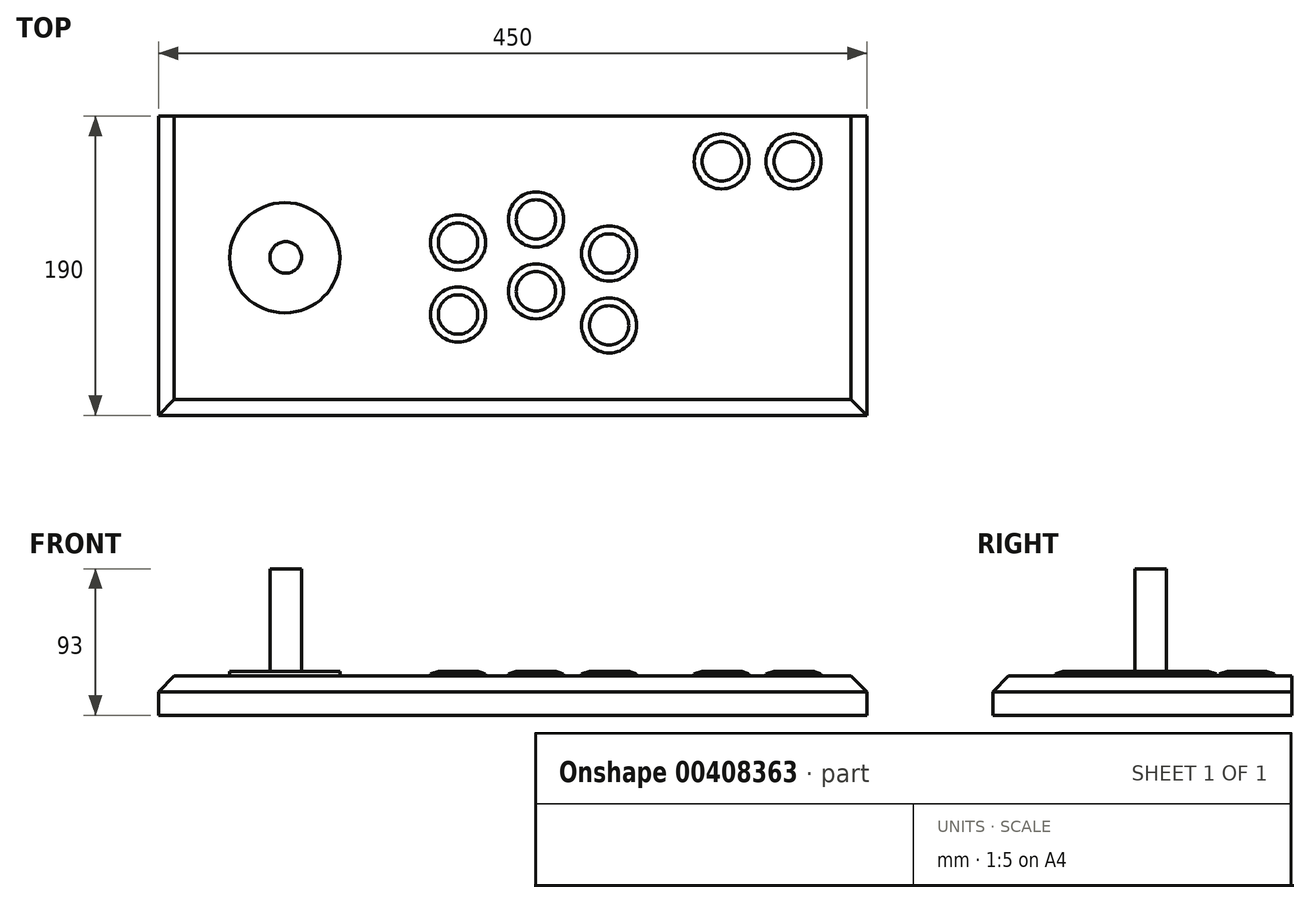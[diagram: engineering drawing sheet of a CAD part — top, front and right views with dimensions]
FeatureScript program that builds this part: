
annotation { "Feature Type Name" : "Feature", "Feature Type Description" : "" }
export const myFeature = defineFeature(function(context is Context, id is Id, definition is map)
    precondition{}
    {
        {
            var Q0;
            Q0=qCreatedBy(makeId("Top.planeOp"),FACE);
            var sketch = newSketch(context, id + "F0", { "sketchPlane" : qUnion([Q0])});
            skLineSegment(sketch, "E0", {"start": v(-232.6, -81.18) * mm, "end": v(217.4, -81.18) * mm});
            skLineSegment(sketch, "E1", {"start": v(-232.6, -81.18) * mm, "end": v(-232.6, 108.82) * mm});
            skLineSegment(sketch, "E2", {"start": v(-232.6, 108.82) * mm, "end": v(217.4, 108.82) * mm});
            skLineSegment(sketch, "E3", {"start": v(217.4, -81.18) * mm, "end": v(217.4, 108.82) * mm});
            skSolve(sketch);
        }
        {
            var Q0;
            Q0=makeQuery(id+"F0.imprint","IMPRINT",FACE,{"disambiguationData":[TD([[makeQuery(id+"F0.imprint","IMPRINT",EDGE,{"derivedFrom":sQuery(id+"F0.wireOp",EDGE,"E0")}),1.0]])]});
            extrude(context, id + "F1", {"entities" : qUnion([Q0]), "depth" : 25 * mm});
        }
        {
            var Q0;
            Q0=makeQuery(id+"F1.opExtrude","CAP_EDGE",EDGE,{"disambiguationData":[OSD([sQuery(id+"F0.wireOp",EDGE,"E1")])],"isStart":false});
            var Q1;
            Q1=makeQuery(id+"F1.opExtrude","CAP_EDGE",EDGE,{"disambiguationData":[OSD([sQuery(id+"F0.wireOp",EDGE,"E3")])],"isStart":false});
            var Q2;
            Q2=makeQuery(id+"F1.opExtrude","CAP_EDGE",EDGE,{"disambiguationData":[OSD([sQuery(id+"F0.wireOp",EDGE,"E0")])],"isStart":false});
            chamfer(context, id + "F2", {"entities" : qUnion([Q0, Q1, Q2]), "width" : 10 * mm, "tangentPropagation" : true});
        }
        {
            var Q0;
            Q0=makeQuery(id+"F1.opExtrude","CAP_FACE",FACE,{"disambiguationData":[OSD([sQuery(id+"F0.wireOp",EDGE,"E0"),sQuery(id+"F0.wireOp",EDGE,"E1"),sQuery(id+"F0.wireOp",EDGE,"E2"),sQuery(id+"F0.wireOp",EDGE,"E3")])],"isStart":false});
            var sketch = newSketch(context, id + "F3", { "sketchPlane" : qUnion([Q0])});
            skCircle(sketch, "E4", {"center": v(-152.3, 18.92) * mm, "radius": 35 * mm});
            skCircle(sketch, "E5", {"center": v(-42.27, 28.55) * mm, "radius": 17.5 * mm});
            skCircle(sketch, "E6", {"center": v(-42.27, -17.12) * mm, "radius": 17.5 * mm});
            skCircle(sketch, "E7", {"center": v(7.22, 43.26) * mm, "radius": 17.5 * mm});
            skCircle(sketch, "E8", {"center": v(7.22, -2.4) * mm, "radius": 17.5 * mm});
            skCircle(sketch, "E9", {"center": v(53.66, 21.62) * mm, "radius": 17.5 * mm});
            skCircle(sketch, "E10", {"center": v(53.66, -24.05) * mm, "radius": 17.5 * mm});
            skCircle(sketch, "E11", {"center": v(170.84, 80.17) * mm, "radius": 17.5 * mm});
            skCircle(sketch, "E12", {"center": v(125.17, 80.17) * mm, "radius": 17.5 * mm});
            skSolve(sketch);
        }
        {
            var Q0;
            Q0=makeQuery(id+"F3.imprint","IMPRINT",FACE,{"disambiguationData":[TD([[makeQuery(id+"F3.imprint","IMPRINT",EDGE,{"derivedFrom":sQuery(id+"F3.wireOp",EDGE,"E4")}),1.0]])]});
            var Q1;
            Q1=makeQuery(id+"F3.imprint","IMPRINT",FACE,{"disambiguationData":[TD([[makeQuery(id+"F3.imprint","IMPRINT",EDGE,{"derivedFrom":sQuery(id+"F3.wireOp",EDGE,"E5")}),1.0]])]});
            var Q2;
            Q2=makeQuery(id+"F3.imprint","IMPRINT",FACE,{"disambiguationData":[TD([[makeQuery(id+"F3.imprint","IMPRINT",EDGE,{"derivedFrom":sQuery(id+"F3.wireOp",EDGE,"E6")}),1.0]])]});
            var Q3;
            Q3=makeQuery(id+"F3.imprint","IMPRINT",FACE,{"disambiguationData":[TD([[makeQuery(id+"F3.imprint","IMPRINT",EDGE,{"derivedFrom":sQuery(id+"F3.wireOp",EDGE,"E7")}),1.0]])]});
            var Q4;
            Q4=makeQuery(id+"F3.imprint","IMPRINT",FACE,{"disambiguationData":[TD([[makeQuery(id+"F3.imprint","IMPRINT",EDGE,{"derivedFrom":sQuery(id+"F3.wireOp",EDGE,"E8")}),1.0]])]});
            var Q5;
            Q5=makeQuery(id+"F3.imprint","IMPRINT",FACE,{"disambiguationData":[TD([[makeQuery(id+"F3.imprint","IMPRINT",EDGE,{"derivedFrom":sQuery(id+"F3.wireOp",EDGE,"E9")}),1.0]])]});
            var Q6;
            Q6=makeQuery(id+"F3.imprint","IMPRINT",FACE,{"disambiguationData":[TD([[makeQuery(id+"F3.imprint","IMPRINT",EDGE,{"derivedFrom":sQuery(id+"F3.wireOp",EDGE,"E11")}),1.0]])]});
            var Q7;
            Q7=makeQuery(id+"F3.imprint","IMPRINT",FACE,{"disambiguationData":[TD([[makeQuery(id+"F3.imprint","IMPRINT",EDGE,{"derivedFrom":sQuery(id+"F3.wireOp",EDGE,"E12")}),1.0]])]});
            var Q8;
            Q8=makeQuery(id+"F3.imprint","IMPRINT",FACE,{"disambiguationData":[TD([[makeQuery(id+"F3.imprint","IMPRINT",EDGE,{"derivedFrom":sQuery(id+"F3.wireOp",EDGE,"E10")}),1.0]])]});
            extrude(context, id + "F4", {"entities" : qUnion([Q0, Q1, Q2, Q3, Q4, Q5, Q6, Q7, Q8]), "operationType" : NewBodyOperationType.ADD, "depth" : 3 * mm});
        }
        {
            var Q0;
            Q0=makeQuery(id+"F4.opExtrude","CAP_FACE",FACE,{"disambiguationData":[OSD([sQuery(id+"F3.wireOp",EDGE,"E5")])],"isStart":false});
            var Q1;
            Q1=makeQuery(id+"F4.opExtrude","CAP_FACE",FACE,{"disambiguationData":[OSD([sQuery(id+"F3.wireOp",EDGE,"E6")])],"isStart":false});
            var Q2;
            Q2=makeQuery(id+"F4.opExtrude","CAP_FACE",FACE,{"disambiguationData":[OSD([sQuery(id+"F3.wireOp",EDGE,"E7")])],"isStart":false});
            var Q3;
            Q3=makeQuery(id+"F4.opExtrude","CAP_FACE",FACE,{"disambiguationData":[OSD([sQuery(id+"F3.wireOp",EDGE,"E8")])],"isStart":false});
            var Q4;
            Q4=makeQuery(id+"F4.opExtrude","CAP_FACE",FACE,{"disambiguationData":[OSD([sQuery(id+"F3.wireOp",EDGE,"E9")])],"isStart":false});
            var Q5;
            Q5=makeQuery(id+"F4.opExtrude","CAP_FACE",FACE,{"disambiguationData":[OSD([sQuery(id+"F3.wireOp",EDGE,"E10")])],"isStart":false});
            var Q6;
            Q6=makeQuery(id+"F4.opExtrude","CAP_FACE",FACE,{"disambiguationData":[OSD([sQuery(id+"F3.wireOp",EDGE,"E11")])],"isStart":false});
            var Q7;
            Q7=makeQuery(id+"F4.opExtrude","CAP_FACE",FACE,{"disambiguationData":[OSD([sQuery(id+"F3.wireOp",EDGE,"E12")])],"isStart":false});
            chamfer(context, id + "F5", {"entities" : qUnion([Q0, Q1, Q2, Q3, Q4, Q5, Q6, Q7]), "chamferType" : ChamferType.OFFSET_ANGLE, "width" : 5 * mm, "oppositeDirection" : false, "angle" : 20 * degree, "tangentPropagation" : true});
        }
        {
            var Q0;
            Q0=makeQuery(id+"F4.opExtrude","CAP_FACE",FACE,{"disambiguationData":[OSD([sQuery(id+"F3.wireOp",EDGE,"E4")])],"isStart":false});
            var sketch = newSketch(context, id + "F6", { "sketchPlane" : qUnion([Q0])});
            skLineSegment(sketch, "E13", {"start": v(-151.7, 19.17) * mm, "end": v(-151.7, 18.92) * mm});
            skCircle(sketch, "E14", {"center": v(-151.7, 19.17) * mm, "radius": 10 * mm});
            skPoint(sketch, "E14.centerSnap0", {"position": v(-151.7, 18.92) * mm});
            skPoint(sketch, "E15.orphan", {"position": v(-151.7, 53.91) * mm});
            skPoint(sketch, "E16.trimOffspring.end.orphan", {"position": v(-151.7, -16.08) * mm});
            skSolve(sketch);
        }
        {
            var Q0;
            Q0=makeQuery(id+"F6.imprint","IMPRINT",FACE,{"disambiguationData":[TD([[makeQuery(id+"F6.imprint","IMPRINT",EDGE,{"derivedFrom":sQuery(id+"F6.wireOp",EDGE,"E14")}),1.0]])]});
            extrude(context, id + "F7", {"entities" : qUnion([Q0]), "operationType" : NewBodyOperationType.ADD, "depth" : 65 * mm});
        }
    });
